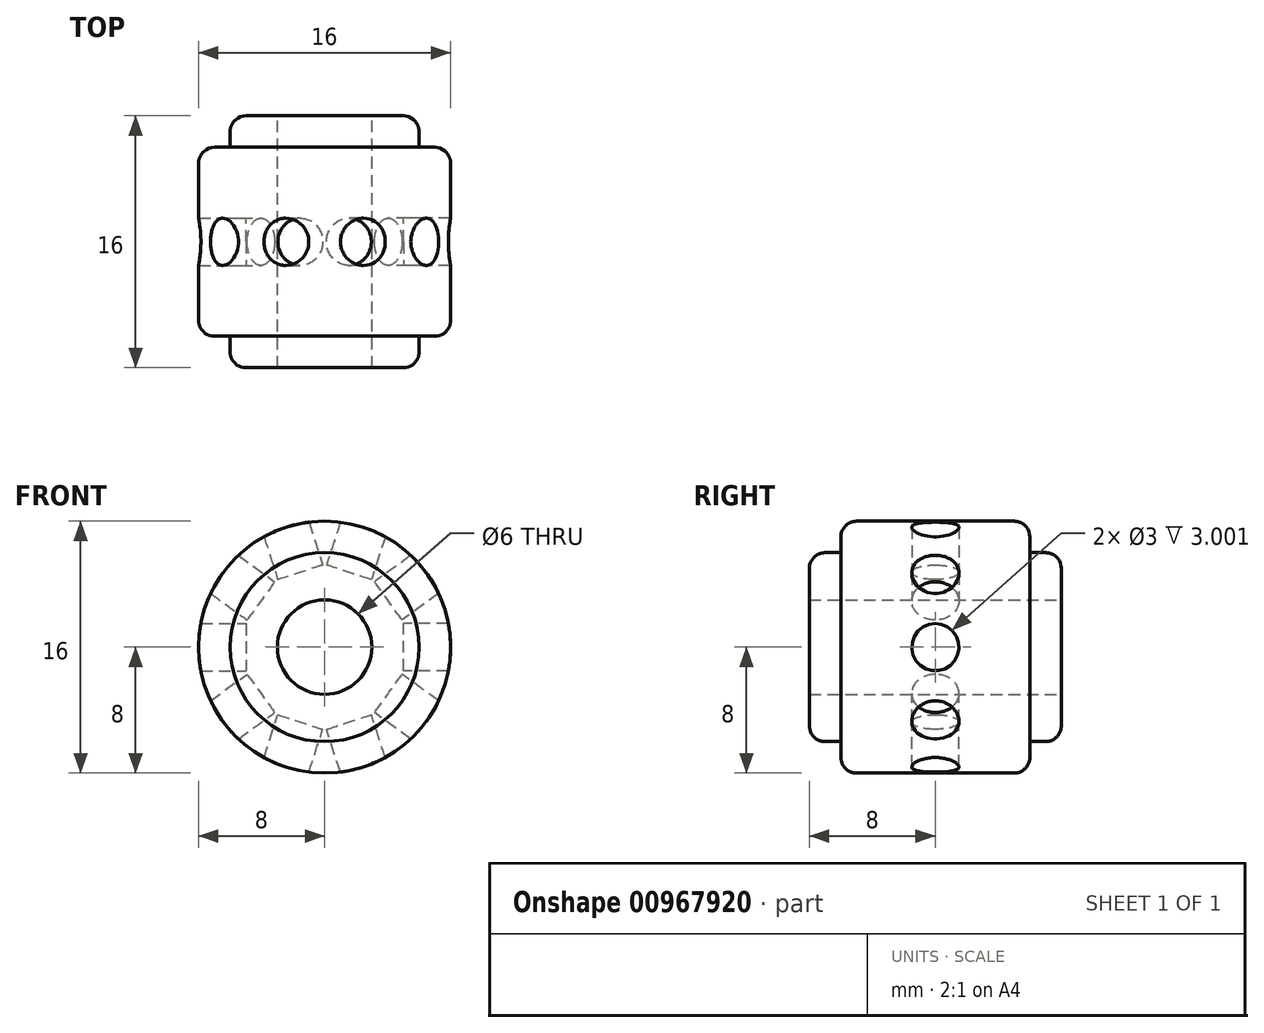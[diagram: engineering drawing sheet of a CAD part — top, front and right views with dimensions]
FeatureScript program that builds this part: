
annotation { "Feature Type Name" : "Feature", "Feature Type Description" : "" }
export const myFeature = defineFeature(function(context is Context, id is Id, definition is map)
    precondition{}
    {
        {
            var Q0;
            Q0=qCreatedBy(makeId("Front.planeOp"),FACE);
            var sketch = newSketch(context, id + "F0", { "sketchPlane" : qUnion([Q0])});
            skCircle(sketch, "E0", {"center": v(0, 0) * mm, "radius": 8 * mm});
            skCircle(sketch, "E1", {"center": v(0, 0) * mm, "radius": 6 * mm});
            skCircle(sketch, "E2", {"center": v(0, 0) * mm, "radius": 3 * mm});
            skSolve(sketch);
        }
        {
            var Q0;
            Q0=makeQuery(id+"F0.imprint","IMPRINT",FACE,{"disambiguationData":[TD([[makeQuery(id+"F0.imprint","IMPRINT",EDGE,{"derivedFrom":sQuery(id+"F0.wireOp",EDGE,"E1")}),1.0]])]});
            extrude(context, id + "F1", {"entities" : qUnion([Q0]), "depth" : 16 * mm, "offsetDistance" : 25 * mm, "symmetric" : true});
        }
        {
            var Q0;
            Q0=makeQuery(id+"F0.imprint","IMPRINT",FACE,{"disambiguationData":[TD([[makeQuery(id+"F0.imprint","IMPRINT",EDGE,{"derivedFrom":sQuery(id+"F0.wireOp",EDGE,"E0")}),1.0]])]});
            extrude(context, id + "F2", {"entities" : qUnion([Q0]), "operationType" : NewBodyOperationType.ADD, "depth" : 12 * mm, "offsetDistance" : 25 * mm, "symmetric" : true});
        }
        {
            var Q0;
            Q0=qCreatedBy(makeId("Right.planeOp"),FACE);
            var sketch = newSketch(context, id + "F3", { "sketchPlane" : qUnion([Q0])});
            skLineSegment(sketch, "E3", {"start": v(-0.31, 0) * mm, "end": v(-3.36, 0) * mm});
            skCircle(sketch, "E4", {"center": v(0, 0) * mm, "radius": 1.5 * mm});
            skSolve(sketch);
        }
        {
            var Q0;
            Q0 = qSketchRegion(id + "F3", true);
            extrude(context, id + "F4", {"entities" : qUnion([Q0]), "depth" : 25 * mm, "offsetDistance" : 25 * mm, "hasSecondDirection" : true, "secondDirectionOppositeDirection" : true, "secondDirectionDepth" : -5 * mm});
        }
        {
            var Q0;
            Q0=makeQuery(id+"F4.opExtrude","SWEPT_BODY",BODY,{"disambiguationData":[OSD([sQuery(id+"F3.wireOp",EDGE,"E4")])]});
            var Q1;
            Q1=sQuery(id+"F3.wireOp",EDGE,"E3");
            circularPattern(context, id + "F5", {"operationType" : NewBodyOperationType.REMOVE, "entities" : qUnion([Q0]), "axis" : qUnion([Q1]), "angle" : 360 * degree, "instanceCount" : 10, "equalSpace" : true});
        }
        {
            var Q0;
            Q0=makeQuery(id+"F1.opExtrude","CAP_EDGE",EDGE,{"disambiguationData":[OSD([sQuery(id+"F0.wireOp",EDGE,"E1")])],"isStart":true});
            var Q1;
            Q1=makeQuery(id+"F2.opExtrude","CAP_EDGE",EDGE,{"disambiguationData":[OSD([sQuery(id+"F0.wireOp",EDGE,"E0")])],"isStart":true});
            var Q2;
            Q2=makeQuery(id+"F1.opExtrude","CAP_EDGE",EDGE,{"disambiguationData":[OSD([sQuery(id+"F0.wireOp",EDGE,"E1")])],"isStart":false});
            var Q3;
            Q3=makeQuery(id+"F2.opExtrude","CAP_EDGE",EDGE,{"disambiguationData":[OSD([sQuery(id+"F0.wireOp",EDGE,"E0")])],"isStart":false});
            fillet(context, id + "F6", {"entities" : qUnion([Q0, Q1, Q2, Q3]), "radius" : 1 * mm, "tangentPropagation" : true, "allowEdgeOverflow" : false});
        }
    });
